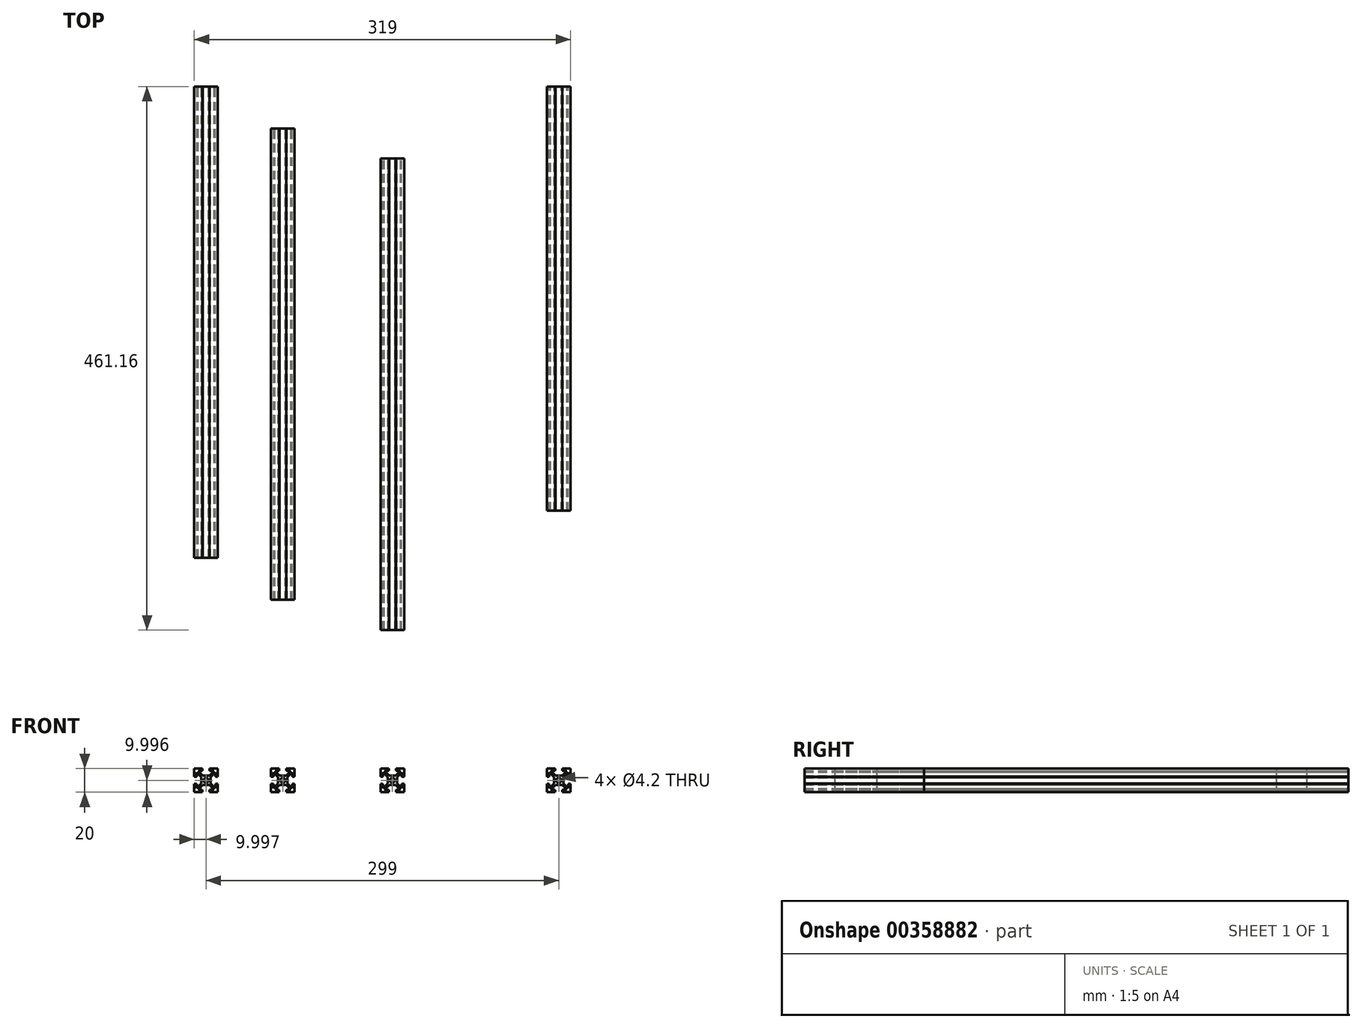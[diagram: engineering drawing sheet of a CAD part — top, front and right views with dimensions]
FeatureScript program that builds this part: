
annotation { "Feature Type Name" : "Feature", "Feature Type Description" : "" }
export const myFeature = defineFeature(function(context is Context, id is Id, definition is map)
    precondition{}
    {
        {
            var Q0;
            Q0=qCreatedBy(makeId("Front.planeOp"),FACE);
            var sketch = newSketch(context, id + "F0", { "sketchPlane" : qUnion([Q0])});
            skLineSegment(sketch, "E0", {"start": v(-3.01, 10) * mm, "end": v(-10.01, 10) * mm});
            skLineSegment(sketch, "E1", {"start": v(-10.01, 10) * mm, "end": v(-10.01, 3) * mm});
            skLineSegment(sketch, "E2", {"start": v(-10.01, 3) * mm, "end": v(-8.01, 3) * mm});
            skLineSegment(sketch, "E3", {"start": v(-8.01, 3) * mm, "end": v(-8.01, 6.75) * mm});
            skLineSegment(sketch, "E4", {"start": v(-8.01, 6.75) * mm, "end": v(-4.01, 2.75) * mm});
            skLineSegment(sketch, "E5", {"start": v(-4.01, 2.75) * mm, "end": v(-4.01, -2.75) * mm});
            skLineSegment(sketch, "E6", {"start": v(-4.01, -2.75) * mm, "end": v(-8.01, -6.75) * mm});
            skLineSegment(sketch, "E7", {"start": v(-8.01, -6.75) * mm, "end": v(-8.01, -3) * mm});
            skLineSegment(sketch, "E8", {"start": v(-8.01, -3) * mm, "end": v(-10.01, -3) * mm});
            skLineSegment(sketch, "E9", {"start": v(-10.01, -3) * mm, "end": v(-10.01, -10) * mm});
            skLineSegment(sketch, "E10", {"start": v(-10.01, -10) * mm, "end": v(-3.01, -10) * mm});
            skLineSegment(sketch, "E11", {"start": v(-3.01, -10) * mm, "end": v(-3.01, -8) * mm});
            skLineSegment(sketch, "E12", {"start": v(-3.01, -8) * mm, "end": v(-6.76, -8) * mm});
            skLineSegment(sketch, "E13", {"start": v(-6.76, -8) * mm, "end": v(-2.76, -4) * mm});
            skLineSegment(sketch, "E14", {"start": v(-2.76, -4) * mm, "end": v(2.86, -4) * mm});
            skLineSegment(sketch, "E15", {"start": v(2.86, -4) * mm, "end": v(6.86, -8) * mm});
            skLineSegment(sketch, "E16", {"start": v(6.86, -8) * mm, "end": v(2.99, -8) * mm});
            skLineSegment(sketch, "E17", {"start": v(2.99, -8) * mm, "end": v(2.99, -10) * mm});
            skLineSegment(sketch, "E18", {"start": v(2.99, -10) * mm, "end": v(9.99, -10) * mm});
            skLineSegment(sketch, "E19", {"start": v(9.99, -10) * mm, "end": v(9.99, -3) * mm});
            skLineSegment(sketch, "E20", {"start": v(9.99, -3) * mm, "end": v(7.99, -3) * mm});
            skLineSegment(sketch, "E21", {"start": v(7.99, -3) * mm, "end": v(7.99, -6.67) * mm});
            skLineSegment(sketch, "E22", {"start": v(7.99, -6.67) * mm, "end": v(3.99, -2.67) * mm});
            skLineSegment(sketch, "E23", {"start": v(3.99, -2.67) * mm, "end": v(3.99, 2.74) * mm});
            skLineSegment(sketch, "E24", {"start": v(3.99, 2.74) * mm, "end": v(7.99, 6.74) * mm});
            skLineSegment(sketch, "E25", {"start": v(7.99, 6.74) * mm, "end": v(7.99, 3) * mm});
            skLineSegment(sketch, "E26", {"start": v(7.99, 3) * mm, "end": v(9.99, 3) * mm});
            skLineSegment(sketch, "E27", {"start": v(9.99, 3) * mm, "end": v(9.99, 10) * mm});
            skLineSegment(sketch, "E28", {"start": v(9.99, 10) * mm, "end": v(2.99, 10) * mm});
            skLineSegment(sketch, "E29", {"start": v(2.99, 10) * mm, "end": v(2.99, 8) * mm});
            skLineSegment(sketch, "E30", {"start": v(2.99, 8) * mm, "end": v(6.86, 8) * mm});
            skLineSegment(sketch, "E31", {"start": v(6.86, 8) * mm, "end": v(2.85, 4) * mm});
            skLineSegment(sketch, "E32", {"start": v(2.85, 4) * mm, "end": v(-2.76, 4) * mm});
            skLineSegment(sketch, "E33", {"start": v(-2.76, 4) * mm, "end": v(-6.76, 8) * mm});
            skLineSegment(sketch, "E34", {"start": v(-6.76, 8) * mm, "end": v(-3.01, 8) * mm});
            skLineSegment(sketch, "E35", {"start": v(-3.01, 8) * mm, "end": v(-3.01, 10) * mm});
            skCircle(sketch, "E36", {"center": v(-0.01, 0) * mm, "radius": 2.1 * mm});
            skSolve(sketch);
        }
        {
            var Q0;
            Q0=makeQuery(id+"F0.imprint","IMPRINT",FACE,{"disambiguationData":[TD([[makeQuery(id+"F0.imprint","IMPRINT",EDGE,{"derivedFrom":sQuery(id+"F0.wireOp",EDGE,"E0")}),1.0]])]});
            extrude(context, id + "F1", {"entities" : qUnion([Q0]), "depth" : 400 * mm, "symmetric" : true});
        }
        {
            var Q0;
            Q0=makeQuery(id+"F1.opExtrude","SWEPT_BODY",BODY,{"disambiguationData":[OSD([sQuery(id+"F0.wireOp",EDGE,"E0"),sQuery(id+"F0.wireOp",EDGE,"E1"),sQuery(id+"F0.wireOp",EDGE,"E2"),sQuery(id+"F0.wireOp",EDGE,"E3"),sQuery(id+"F0.wireOp",EDGE,"E4"),sQuery(id+"F0.wireOp",EDGE,"E5"),sQuery(id+"F0.wireOp",EDGE,"E6"),sQuery(id+"F0.wireOp",EDGE,"E7"),sQuery(id+"F0.wireOp",EDGE,"E8"),sQuery(id+"F0.wireOp",EDGE,"E9"),sQuery(id+"F0.wireOp",EDGE,"E10"),sQuery(id+"F0.wireOp",EDGE,"E11"),sQuery(id+"F0.wireOp",EDGE,"E12"),sQuery(id+"F0.wireOp",EDGE,"E13"),sQuery(id+"F0.wireOp",EDGE,"E14"),sQuery(id+"F0.wireOp",EDGE,"E15"),sQuery(id+"F0.wireOp",EDGE,"E16"),sQuery(id+"F0.wireOp",EDGE,"E17"),sQuery(id+"F0.wireOp",EDGE,"E18"),sQuery(id+"F0.wireOp",EDGE,"E19"),sQuery(id+"F0.wireOp",EDGE,"E20"),sQuery(id+"F0.wireOp",EDGE,"E21"),sQuery(id+"F0.wireOp",EDGE,"E22"),sQuery(id+"F0.wireOp",EDGE,"E23"),sQuery(id+"F0.wireOp",EDGE,"E24"),sQuery(id+"F0.wireOp",EDGE,"E25"),sQuery(id+"F0.wireOp",EDGE,"E26"),sQuery(id+"F0.wireOp",EDGE,"E27"),sQuery(id+"F0.wireOp",EDGE,"E28"),sQuery(id+"F0.wireOp",EDGE,"E29"),sQuery(id+"F0.wireOp",EDGE,"E30"),sQuery(id+"F0.wireOp",EDGE,"E31"),sQuery(id+"F0.wireOp",EDGE,"E32"),sQuery(id+"F0.wireOp",EDGE,"E33"),sQuery(id+"F0.wireOp",EDGE,"E34"),sQuery(id+"F0.wireOp",EDGE,"E35"),sQuery(id+"F0.wireOp",EDGE,"E36")])]});
            transform(context, id + "F2", {"entities" : qUnion([Q0]), "transformType" : TransformType.TRANSLATION_3D, "dx" : 65.08 * mm, "dy" : -35.53 * mm, "dz" : 0 * mm, "makeCopy" : true});
        }
        {
            var Q0;
            Q0=makeQuery(id+"F2.opPattern","COPY",BODY,{"derivedFrom":makeQuery(id+"F1.opExtrude","SWEPT_BODY",BODY,{"disambiguationData":[OSD([sQuery(id+"F0.wireOp",EDGE,"E0"),sQuery(id+"F0.wireOp",EDGE,"E1"),sQuery(id+"F0.wireOp",EDGE,"E2"),sQuery(id+"F0.wireOp",EDGE,"E3"),sQuery(id+"F0.wireOp",EDGE,"E4"),sQuery(id+"F0.wireOp",EDGE,"E5"),sQuery(id+"F0.wireOp",EDGE,"E6"),sQuery(id+"F0.wireOp",EDGE,"E7"),sQuery(id+"F0.wireOp",EDGE,"E8"),sQuery(id+"F0.wireOp",EDGE,"E9"),sQuery(id+"F0.wireOp",EDGE,"E10"),sQuery(id+"F0.wireOp",EDGE,"E11"),sQuery(id+"F0.wireOp",EDGE,"E12"),sQuery(id+"F0.wireOp",EDGE,"E13"),sQuery(id+"F0.wireOp",EDGE,"E14"),sQuery(id+"F0.wireOp",EDGE,"E15"),sQuery(id+"F0.wireOp",EDGE,"E16"),sQuery(id+"F0.wireOp",EDGE,"E17"),sQuery(id+"F0.wireOp",EDGE,"E18"),sQuery(id+"F0.wireOp",EDGE,"E19"),sQuery(id+"F0.wireOp",EDGE,"E20"),sQuery(id+"F0.wireOp",EDGE,"E21"),sQuery(id+"F0.wireOp",EDGE,"E22"),sQuery(id+"F0.wireOp",EDGE,"E23"),sQuery(id+"F0.wireOp",EDGE,"E24"),sQuery(id+"F0.wireOp",EDGE,"E25"),sQuery(id+"F0.wireOp",EDGE,"E26"),sQuery(id+"F0.wireOp",EDGE,"E27"),sQuery(id+"F0.wireOp",EDGE,"E28"),sQuery(id+"F0.wireOp",EDGE,"E29"),sQuery(id+"F0.wireOp",EDGE,"E30"),sQuery(id+"F0.wireOp",EDGE,"E31"),sQuery(id+"F0.wireOp",EDGE,"E32"),sQuery(id+"F0.wireOp",EDGE,"E33"),sQuery(id+"F0.wireOp",EDGE,"E34"),sQuery(id+"F0.wireOp",EDGE,"E35"),sQuery(id+"F0.wireOp",EDGE,"E36")])]}),"instanceName":"1"});
            transform(context, id + "F3", {"entities" : qUnion([Q0]), "transformType" : TransformType.TRANSLATION_3D, "dx" : 92.84 * mm, "dy" : -25.64 * mm, "dz" : 0 * mm, "makeCopy" : true});
        }
        {
            var Q0;
            Q0=makeQuery(id+"F1.opExtrude","SWEPT_BODY",BODY,{"disambiguationData":[OSD([sQuery(id+"F0.wireOp",EDGE,"E0"),sQuery(id+"F0.wireOp",EDGE,"E1"),sQuery(id+"F0.wireOp",EDGE,"E2"),sQuery(id+"F0.wireOp",EDGE,"E3"),sQuery(id+"F0.wireOp",EDGE,"E4"),sQuery(id+"F0.wireOp",EDGE,"E5"),sQuery(id+"F0.wireOp",EDGE,"E6"),sQuery(id+"F0.wireOp",EDGE,"E7"),sQuery(id+"F0.wireOp",EDGE,"E8"),sQuery(id+"F0.wireOp",EDGE,"E9"),sQuery(id+"F0.wireOp",EDGE,"E10"),sQuery(id+"F0.wireOp",EDGE,"E11"),sQuery(id+"F0.wireOp",EDGE,"E12"),sQuery(id+"F0.wireOp",EDGE,"E13"),sQuery(id+"F0.wireOp",EDGE,"E14"),sQuery(id+"F0.wireOp",EDGE,"E15"),sQuery(id+"F0.wireOp",EDGE,"E16"),sQuery(id+"F0.wireOp",EDGE,"E17"),sQuery(id+"F0.wireOp",EDGE,"E18"),sQuery(id+"F0.wireOp",EDGE,"E19"),sQuery(id+"F0.wireOp",EDGE,"E20"),sQuery(id+"F0.wireOp",EDGE,"E21"),sQuery(id+"F0.wireOp",EDGE,"E22"),sQuery(id+"F0.wireOp",EDGE,"E23"),sQuery(id+"F0.wireOp",EDGE,"E24"),sQuery(id+"F0.wireOp",EDGE,"E25"),sQuery(id+"F0.wireOp",EDGE,"E26"),sQuery(id+"F0.wireOp",EDGE,"E27"),sQuery(id+"F0.wireOp",EDGE,"E28"),sQuery(id+"F0.wireOp",EDGE,"E29"),sQuery(id+"F0.wireOp",EDGE,"E30"),sQuery(id+"F0.wireOp",EDGE,"E31"),sQuery(id+"F0.wireOp",EDGE,"E32"),sQuery(id+"F0.wireOp",EDGE,"E33"),sQuery(id+"F0.wireOp",EDGE,"E34"),sQuery(id+"F0.wireOp",EDGE,"E35"),sQuery(id+"F0.wireOp",EDGE,"E36")])]});
            transform(context, id + "F4", {"entities" : qUnion([Q0]), "transformType" : TransformType.TRANSLATION_3D, "dx" : 299 * mm, "dy" : 0 * mm, "dz" : 0 * mm, "makeCopy" : true});
        }
        {
            var Q0;
            Q0=makeQuery(id+"F4.opPattern","COPY",FACE,{"derivedFrom":makeQuery(id+"F1.opExtrude","CAP_FACE",FACE,{"disambiguationData":[OSD([sQuery(id+"F0.wireOp",EDGE,"E0"),sQuery(id+"F0.wireOp",EDGE,"E1"),sQuery(id+"F0.wireOp",EDGE,"E2"),sQuery(id+"F0.wireOp",EDGE,"E3"),sQuery(id+"F0.wireOp",EDGE,"E4"),sQuery(id+"F0.wireOp",EDGE,"E5"),sQuery(id+"F0.wireOp",EDGE,"E6"),sQuery(id+"F0.wireOp",EDGE,"E7"),sQuery(id+"F0.wireOp",EDGE,"E8"),sQuery(id+"F0.wireOp",EDGE,"E9"),sQuery(id+"F0.wireOp",EDGE,"E10"),sQuery(id+"F0.wireOp",EDGE,"E11"),sQuery(id+"F0.wireOp",EDGE,"E12"),sQuery(id+"F0.wireOp",EDGE,"E13"),sQuery(id+"F0.wireOp",EDGE,"E14"),sQuery(id+"F0.wireOp",EDGE,"E15"),sQuery(id+"F0.wireOp",EDGE,"E16"),sQuery(id+"F0.wireOp",EDGE,"E17"),sQuery(id+"F0.wireOp",EDGE,"E18"),sQuery(id+"F0.wireOp",EDGE,"E19"),sQuery(id+"F0.wireOp",EDGE,"E20"),sQuery(id+"F0.wireOp",EDGE,"E21"),sQuery(id+"F0.wireOp",EDGE,"E22"),sQuery(id+"F0.wireOp",EDGE,"E23"),sQuery(id+"F0.wireOp",EDGE,"E24"),sQuery(id+"F0.wireOp",EDGE,"E25"),sQuery(id+"F0.wireOp",EDGE,"E26"),sQuery(id+"F0.wireOp",EDGE,"E27"),sQuery(id+"F0.wireOp",EDGE,"E28"),sQuery(id+"F0.wireOp",EDGE,"E29"),sQuery(id+"F0.wireOp",EDGE,"E30"),sQuery(id+"F0.wireOp",EDGE,"E31"),sQuery(id+"F0.wireOp",EDGE,"E32"),sQuery(id+"F0.wireOp",EDGE,"E33"),sQuery(id+"F0.wireOp",EDGE,"E34"),sQuery(id+"F0.wireOp",EDGE,"E35"),sQuery(id+"F0.wireOp",EDGE,"E36")])],"isStart":false}),"instanceName":"1"});
            extrude(context, id + "F5", {"entities" : qUnion([Q0]), "operationType" : NewBodyOperationType.REMOVE, "oppositeDirection" : true, "depth" : 40 * mm});
        }
    });
